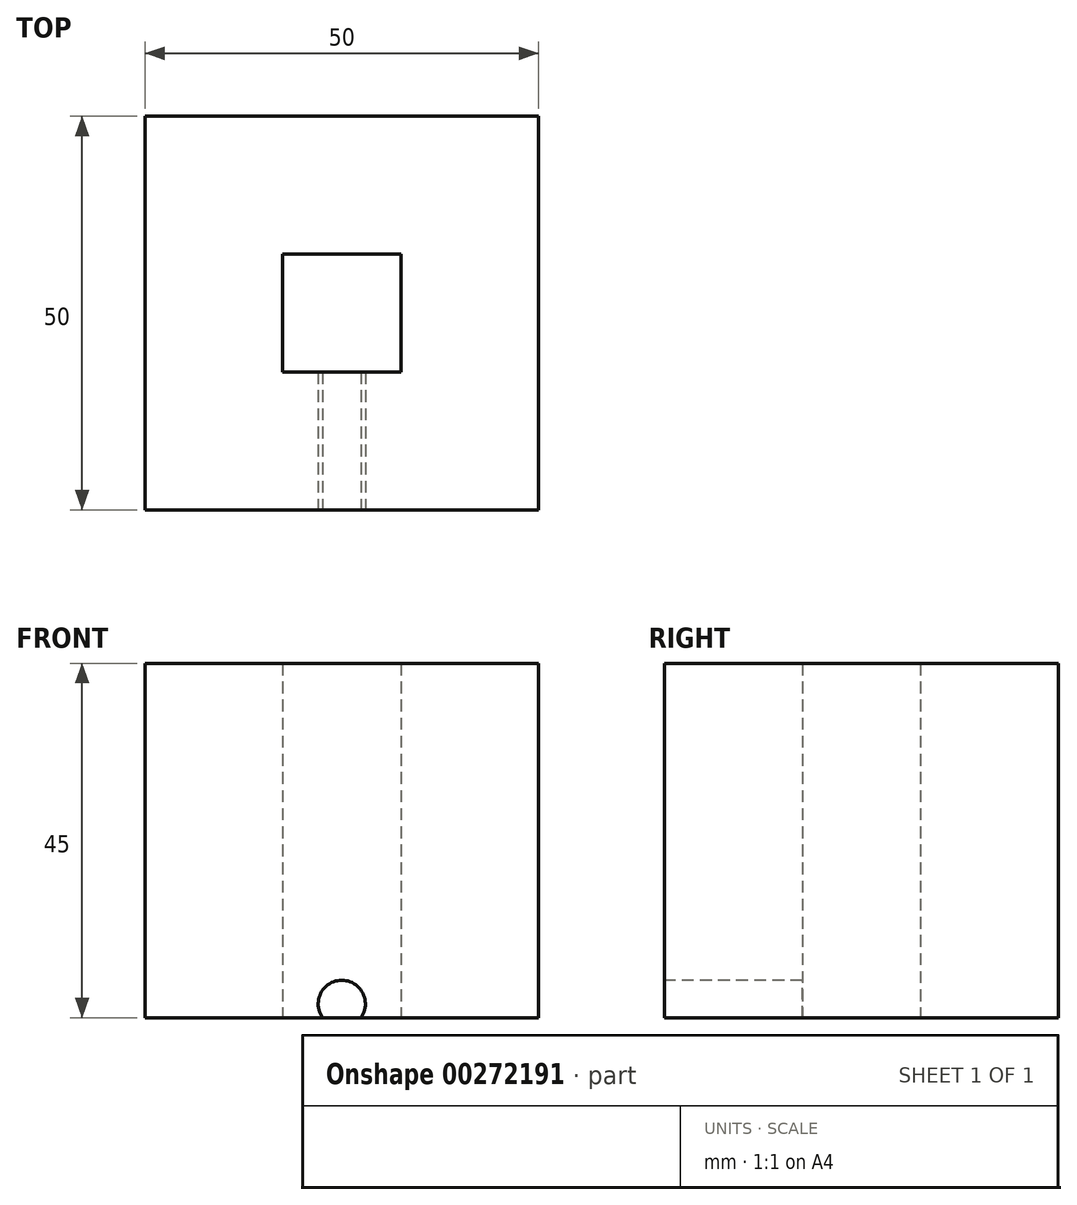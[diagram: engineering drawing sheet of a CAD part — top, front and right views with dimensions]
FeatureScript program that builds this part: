
annotation { "Feature Type Name" : "Feature", "Feature Type Description" : "" }
export const myFeature = defineFeature(function(context is Context, id is Id, definition is map)
    precondition{}
    {
        {
            var Q0;
            Q0=qCreatedBy(makeId("Top.planeOp"),FACE);
            var sketch = newSketch(context, id + "F0", { "sketchPlane" : qUnion([Q0])});
            skLineSegment(sketch, "E0.bottom", {"start": v(-25, 25) * mm, "end": v(25, 25) * mm});
            skLineSegment(sketch, "E0.top", {"start": v(-25, -25) * mm, "end": v(25, -25) * mm});
            skLineSegment(sketch, "E0.left", {"start": v(-25, 25) * mm, "end": v(-25, -25) * mm});
            skLineSegment(sketch, "E0.right", {"start": v(25, 25) * mm, "end": v(25, -25) * mm});
            skLineSegment(sketch, "E1.bottom", {"start": v(-7.5, 7.5) * mm, "end": v(7.5, 7.5) * mm});
            skLineSegment(sketch, "E1.top", {"start": v(-7.5, -7.5) * mm, "end": v(7.5, -7.5) * mm});
            skLineSegment(sketch, "E1.left", {"start": v(-7.5, 7.5) * mm, "end": v(-7.5, -7.5) * mm});
            skLineSegment(sketch, "E1.right", {"start": v(7.5, 7.5) * mm, "end": v(7.5, -7.5) * mm});
            skSolve(sketch);
        }
        {
            var Q0;
            Q0=makeQuery(id+"F0.imprint","IMPRINT",FACE,{"disambiguationData":[TD([[makeQuery(id+"F0.imprint","IMPRINT",EDGE,{"derivedFrom":sQuery(id+"F0.wireOp",EDGE,"E0.bottom")}),-1.0]])]});
            extrude(context, id + "F1", {"entities" : qUnion([Q0]), "depth" : 45 * mm});
        }
        {
            var Q0;
            Q0=makeQuery(id+"F1.opExtrude","SWEPT_FACE",FACE,{"disambiguationData":[OSD([sQuery(id+"F0.wireOp",EDGE,"E0.top")])]});
            var sketch = newSketch(context, id + "F2", { "sketchPlane" : qUnion([Q0])});
            skCircle(sketch, "E2", {"center": v(0, 1.75) * mm, "radius": 3 * mm});
            skSolve(sketch);
        }
        {
            var Q0;
            {var subQ0=sQuery(id+"F2.wireOp",EDGE,"E2");var subQ1=makeQuery(id+"F1.opExtrude","CAP_EDGE",EDGE,{"disambiguationData":[OSD([sQuery(id+"F0.wireOp",EDGE,"E0.top")])],"isStart":true});var subQ2=makeQuery(id+"F2.imprint","INTERSECT",VERTEX,{"disambiguationData":[OD(0.0)],"derivedFrom":[subQ1,subQ0]});Q0=makeQuery(id+"F2.imprint","IMPRINT",FACE,{"disambiguationData":[TD([[makeQuery(id+"F2.imprint","IMPRINT",EDGE,{"disambiguationData":[TD([[subQ2,1.0]])],"derivedFrom":subQ0}),1.0]])]});}
            extrude(context, id + "F3", {"entities" : qUnion([Q0]), "operationType" : NewBodyOperationType.REMOVE, "oppositeDirection" : true, "depth" : 25 * mm});
        }
    });
